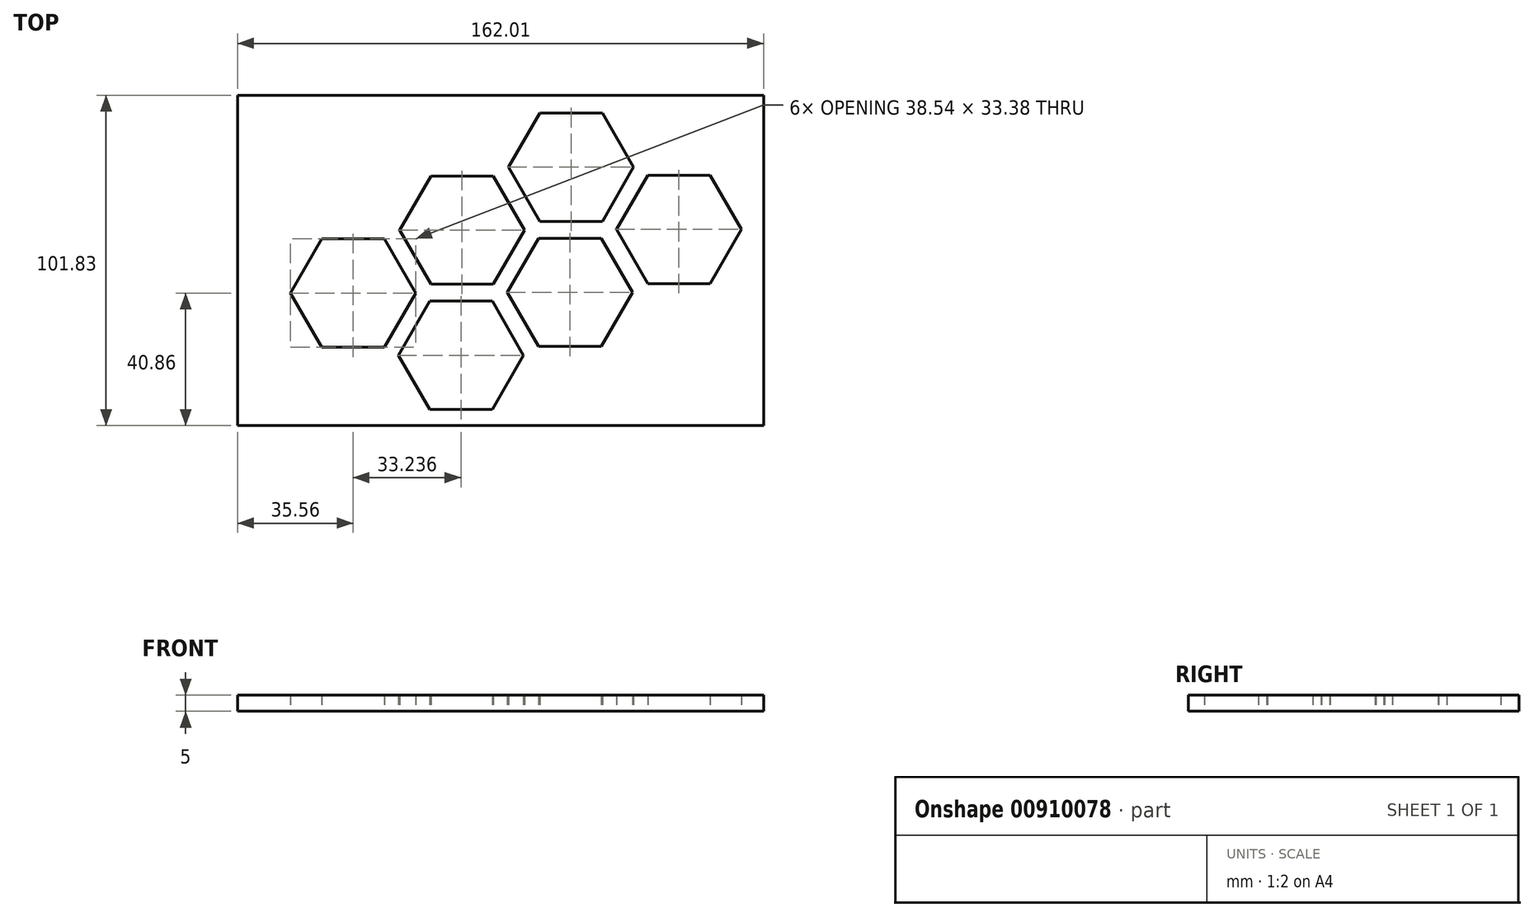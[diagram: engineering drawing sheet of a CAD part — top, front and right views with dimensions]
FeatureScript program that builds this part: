
annotation { "Feature Type Name" : "Feature", "Feature Type Description" : "" }
export const myFeature = defineFeature(function(context is Context, id is Id, definition is map)
    precondition{}
    {
        {
            var Q0;
            Q0=qCreatedBy(makeId("Top.planeOp"),FACE);
            var sketch = newSketch(context, id + "F0", { "sketchPlane" : qUnion([Q0])});
            skCircle(sketch, "E0.cCircle", {"center": v(0, 0) * mm, "radius": 16.69 * mm, "construction": true});
            skLineSegment(sketch, "E0.0", {"start": v(9.64, -16.69) * mm, "end": v(-9.64, -16.69) * mm});
            skLineSegment(sketch, "E0.1", {"start": v(-9.64, -16.69) * mm, "end": v(-19.27, 0) * mm});
            skLineSegment(sketch, "E0.2", {"start": v(-19.27, 0) * mm, "end": v(-9.64, 16.69) * mm});
            skLineSegment(sketch, "E0.3", {"start": v(-9.64, 16.69) * mm, "end": v(9.64, 16.69) * mm});
            skLineSegment(sketch, "E0.4", {"start": v(9.64, 16.69) * mm, "end": v(19.27, 0) * mm});
            skLineSegment(sketch, "E0.5", {"start": v(19.27, 0) * mm, "end": v(9.64, -16.69) * mm});
            skPoint(sketch, "E0.0.midPoint", {"position": v(0, -16.69) * mm});
            skCircle(sketch, "E1.cCircle", {"center": v(33.24, -19.19) * mm, "radius": 16.69 * mm, "construction": true});
            skLineSegment(sketch, "E1.0", {"start": v(23.6, -2.5) * mm, "end": v(42.87, -2.5) * mm});
            skLineSegment(sketch, "E1.1", {"start": v(42.87, -2.5) * mm, "end": v(52.5, -19.19) * mm});
            skLineSegment(sketch, "E1.2", {"start": v(52.5, -19.19) * mm, "end": v(42.87, -35.88) * mm});
            skLineSegment(sketch, "E1.3", {"start": v(42.87, -35.88) * mm, "end": v(23.6, -35.88) * mm});
            skLineSegment(sketch, "E1.4", {"start": v(23.6, -35.88) * mm, "end": v(13.97, -19.19) * mm});
            skLineSegment(sketch, "E1.5", {"start": v(13.97, -19.19) * mm, "end": v(23.6, -2.5) * mm});
            skPoint(sketch, "E1.0.midPoint", {"position": v(33.24, -2.5) * mm});
            skCircle(sketch, "E2.1.0.0", {"center": v(33.58, 19.38) * mm, "radius": 16.69 * mm, "construction": true});
            skPoint(sketch, "E2.1.0.1", {"position": v(33.58, 2.7) * mm});
            skLineSegment(sketch, "E2.1.0.2", {"start": v(23.94, 2.7) * mm, "end": v(14.3, 19.38) * mm});
            skPoint(sketch, "E2.1.0.3", {"position": v(66.81, 16.89) * mm});
            skLineSegment(sketch, "E2.1.0.4", {"start": v(76.45, -16.5) * mm, "end": v(57.18, -16.5) * mm});
            skLineSegment(sketch, "E2.1.0.5", {"start": v(43.21, 36.07) * mm, "end": v(52.85, 19.38) * mm});
            skLineSegment(sketch, "E2.1.0.6", {"start": v(76.45, 16.89) * mm, "end": v(86.08, 0.2) * mm});
            skLineSegment(sketch, "E2.1.0.7", {"start": v(86.08, 0.2) * mm, "end": v(76.45, -16.5) * mm});
            skLineSegment(sketch, "E2.1.0.8", {"start": v(47.54, 0.2) * mm, "end": v(57.18, 16.89) * mm});
            skLineSegment(sketch, "E2.1.0.9", {"start": v(52.85, 19.39) * mm, "end": v(43.21, 2.7) * mm});
            skCircle(sketch, "E2.1.0.10", {"center": v(66.81, 0.2) * mm, "radius": 16.69 * mm, "construction": true});
            skLineSegment(sketch, "E2.1.0.11", {"start": v(43.21, 2.7) * mm, "end": v(23.94, 2.7) * mm});
            skLineSegment(sketch, "E2.1.0.12", {"start": v(23.94, 36.07) * mm, "end": v(43.21, 36.07) * mm});
            skLineSegment(sketch, "E2.1.0.13", {"start": v(14.3, 19.39) * mm, "end": v(23.94, 36.07) * mm});
            skLineSegment(sketch, "E2.1.0.14", {"start": v(57.18, 16.89) * mm, "end": v(76.45, 16.89) * mm});
            skLineSegment(sketch, "E2.1.0.15", {"start": v(57.18, -16.5) * mm, "end": v(47.54, 0.2) * mm});
            skCircle(sketch, "E2.2.0.0", {"center": v(67.15, 38.77) * mm, "radius": 16.69 * mm, "construction": true});
            skPoint(sketch, "E2.2.0.1", {"position": v(67.15, 22.08) * mm});
            skLineSegment(sketch, "E2.2.0.2", {"start": v(57.52, 22.08) * mm, "end": v(47.88, 38.77) * mm});
            skPoint(sketch, "E2.2.0.3", {"position": v(100.39, 36.27) * mm});
            skLineSegment(sketch, "E2.2.0.4", {"start": v(110.02, 2.9) * mm, "end": v(90.75, 2.9) * mm});
            skLineSegment(sketch, "E2.2.0.5", {"start": v(76.79, 55.46) * mm, "end": v(86.42, 38.77) * mm});
            skLineSegment(sketch, "E2.2.0.6", {"start": v(110.02, 36.27) * mm, "end": v(119.66, 19.58) * mm});
            skLineSegment(sketch, "E2.2.0.7", {"start": v(119.66, 19.58) * mm, "end": v(110.02, 2.9) * mm});
            skLineSegment(sketch, "E2.2.0.8", {"start": v(81.12, 19.58) * mm, "end": v(90.75, 36.27) * mm});
            skLineSegment(sketch, "E2.2.0.9", {"start": v(86.42, 38.77) * mm, "end": v(76.79, 22.08) * mm});
            skCircle(sketch, "E2.2.0.10", {"center": v(100.39, 19.58) * mm, "radius": 16.69 * mm, "construction": true});
            skLineSegment(sketch, "E2.2.0.11", {"start": v(76.79, 22.08) * mm, "end": v(57.52, 22.08) * mm});
            skLineSegment(sketch, "E2.2.0.12", {"start": v(57.52, 55.46) * mm, "end": v(76.79, 55.46) * mm});
            skLineSegment(sketch, "E2.2.0.13", {"start": v(47.88, 38.77) * mm, "end": v(57.52, 55.46) * mm});
            skLineSegment(sketch, "E2.2.0.14", {"start": v(90.75, 36.27) * mm, "end": v(110.02, 36.27) * mm});
            skLineSegment(sketch, "E2.2.0.15", {"start": v(90.75, 2.9) * mm, "end": v(81.12, 19.58) * mm});
            skLineSegment(sketch, "E2.direction1", {"start": v(-9.64, -16.69) * mm, "end": v(23.94, 2.7) * mm, "construction": true});
            skSolve(sketch);
        }
        {
            var Q0;
            Q0=qCreatedBy(makeId("Top.planeOp"),FACE);
            var sketch = newSketch(context, id + "F1", { "sketchPlane" : qUnion([Q0])});
            skLineSegment(sketch, "E3.bottom", {"start": v(-35.56, 60.97) * mm, "end": v(126.45, 60.97) * mm});
            skLineSegment(sketch, "E3.top", {"start": v(-35.56, -40.86) * mm, "end": v(126.45, -40.86) * mm});
            skLineSegment(sketch, "E3.left", {"start": v(-35.56, 60.97) * mm, "end": v(-35.56, -40.86) * mm});
            skLineSegment(sketch, "E3.right", {"start": v(126.45, 60.97) * mm, "end": v(126.45, -40.86) * mm});
            skSolve(sketch);
        }
        {
            var Q0;
            Q0=makeQuery(id+"F1.imprint","IMPRINT",FACE,{"disambiguationData":[TD([[makeQuery(id+"F1.imprint","IMPRINT",EDGE,{"derivedFrom":sQuery(id+"F1.wireOp",EDGE,"E3.bottom")}),-1.0]])]});
            extrude(context, id + "F2", {"entities" : qUnion([Q0]), "depth" : 5 * mm, "offsetDistance" : 25 * mm});
        }
        {
            var Q0;
            Q0=makeQuery(id+"F0.imprint","IMPRINT",FACE,{"disambiguationData":[TD([[makeQuery(id+"F0.imprint","IMPRINT",EDGE,{"derivedFrom":sQuery(id+"F0.wireOp",EDGE,"E0.0")}),-1.0]])]});
            var Q1;
            Q1=makeQuery(id+"F0.imprint","IMPRINT",FACE,{"disambiguationData":[TD([[makeQuery(id+"F0.imprint","IMPRINT",EDGE,{"derivedFrom":sQuery(id+"F0.wireOp",EDGE,"E1.0")}),-1.0]])]});
            var Q2;
            Q2=makeQuery(id+"F0.imprint","IMPRINT",FACE,{"disambiguationData":[TD([[makeQuery(id+"F0.imprint","IMPRINT",EDGE,{"derivedFrom":sQuery(id+"F0.wireOp",EDGE,"E2.1.0.2")}),-1.0]])]});
            var Q3;
            Q3=makeQuery(id+"F0.imprint","IMPRINT",FACE,{"disambiguationData":[TD([[makeQuery(id+"F0.imprint","IMPRINT",EDGE,{"derivedFrom":sQuery(id+"F0.wireOp",EDGE,"E2.1.0.4")}),-1.0]])]});
            var Q4;
            Q4=makeQuery(id+"F0.imprint","IMPRINT",FACE,{"disambiguationData":[TD([[makeQuery(id+"F0.imprint","IMPRINT",EDGE,{"derivedFrom":sQuery(id+"F0.wireOp",EDGE,"E2.2.0.2")}),-1.0]])]});
            var Q5;
            Q5=makeQuery(id+"F0.imprint","IMPRINT",FACE,{"disambiguationData":[TD([[makeQuery(id+"F0.imprint","IMPRINT",EDGE,{"derivedFrom":sQuery(id+"F0.wireOp",EDGE,"E2.2.0.4")}),-1.0]])]});
            extrude(context, id + "F3", {"entities" : qUnion([Q0, Q1, Q2, Q3, Q4, Q5]), "operationType" : NewBodyOperationType.REMOVE, "endBound" : BoundingType.THROUGH_ALL, "depth" : 25 * mm, "offsetDistance" : 25 * mm});
        }
    });
